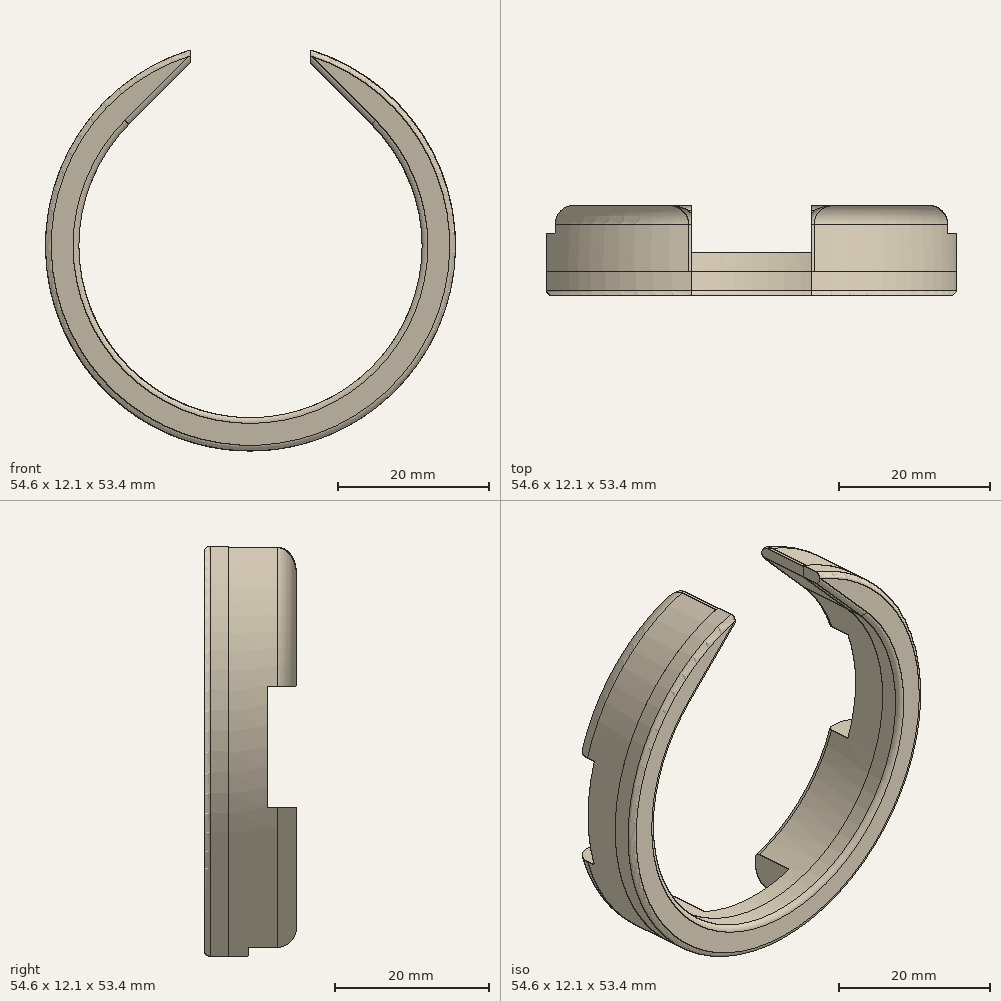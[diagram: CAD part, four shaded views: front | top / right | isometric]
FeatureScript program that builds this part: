
annotation { "Feature Type Name" : "Feature", "Feature Type Description" : "" }
export const myFeature = defineFeature(function(context is Context, id is Id, definition is map)
    precondition{}
    {
        {
            var Q0;
            Q0=qCreatedBy(makeId("Front.planeOp"),FACE);
            var sketch = newSketch(context, id + "F0", { "sketchPlane" : qUnion([Q0])});
            skArc(sketch, "E0", {"start": v(-16.16, 16.16) * mm, "mid": v(0, -22.86) * mm, "end": v(16.16, 16.16) * mm});
            skArc(sketch, "E1", {"start": v(-7.94, 26.13) * mm, "mid": v(0, -27.3) * mm, "end": v(7.94, 26.13) * mm});
            skLineSegment(sketch, "E2", {"start": v(7.94, 24.4) * mm, "end": v(7.94, 26.13) * mm});
            skLineSegment(sketch, "E3", {"start": v(0, 0) * mm, "end": v(0, 106.1) * mm, "construction": true});
            skLineSegment(sketch, "E4.MirrorCS", {"start": v(-7.94, 24.4) * mm, "end": v(-7.94, 26.13) * mm});
            skPoint(sketch, "E5.orphan", {"position": v(-7.94, 49.98) * mm});
            skPoint(sketch, "E6.orphan", {"position": v(7.94, 49.98) * mm});
            skPoint(sketch, "E7.orphan", {"position": v(7.94, 14.4) * mm});
            skPoint(sketch, "E8.orphan", {"position": v(-7.94, 14.4) * mm});
            skLineSegment(sketch, "E9", {"start": v(7.94, 24.4) * mm, "end": v(16.16, 16.16) * mm});
            skLineSegment(sketch, "E10.MirrorCS", {"start": v(-7.94, 24.4) * mm, "end": v(-16.16, 16.16) * mm});
            skPoint(sketch, "E11.orphan", {"position": v(17.29, 49.62) * mm});
            skPoint(sketch, "E12.orphan", {"position": v(-17.29, 49.62) * mm});
            skSolve(sketch);
        }
        {
            var Q0;
            Q0=makeQuery(id+"F0.imprint","IMPRINT",FACE,{"disambiguationData":[TD([[makeQuery(id+"F0.imprint","IMPRINT",EDGE,{"derivedFrom":sQuery(id+"F0.wireOp",EDGE,"E0")}),-1.0]])]});
            extrude(context, id + "F1", {"entities" : qUnion([Q0]), "depth" : 3.17 * mm});
        }
        {
            var Q0;
            Q0=makeQuery(id+"F1.opExtrude","CAP_FACE",FACE,{"disambiguationData":[OSD([sQuery(id+"F0.wireOp",EDGE,"E0"),sQuery(id+"F0.wireOp",EDGE,"E1"),sQuery(id+"F0.wireOp",EDGE,"E2"),sQuery(id+"F0.wireOp",EDGE,"E4.MirrorCS"),sQuery(id+"F0.wireOp",EDGE,"E9"),sQuery(id+"F0.wireOp",EDGE,"E10.MirrorCS")])],"isStart":true});
            extrude(context, id + "F2", {"entities" : qUnion([Q0]), "depth" : 8.9 * mm});
        }
        {
            var Q0;
            Q0=makeQuery(id+"F2.opExtrude","CAP_FACE",FACE,{"disambiguationData":[OSD([sQuery(id+"F0.wireOp",EDGE,"E0"),sQuery(id+"F0.wireOp",EDGE,"E1"),sQuery(id+"F0.wireOp",EDGE,"E2"),sQuery(id+"F0.wireOp",EDGE,"E4.MirrorCS"),sQuery(id+"F0.wireOp",EDGE,"E9"),sQuery(id+"F0.wireOp",EDGE,"E10.MirrorCS")])],"isStart":false});
            var sketch = newSketch(context, id + "F3", { "sketchPlane" : qUnion([Q0])});
            skLineSegment(sketch, "E13", {"start": v(0, 0) * mm, "end": v(0, -47.18) * mm, "construction": true});
            skLineSegment(sketch, "E14", {"start": v(-7.94, -17.24) * mm, "end": v(-7.94, -39.33) * mm});
            skLineSegment(sketch, "E15", {"start": v(-7.94, -39.33) * mm, "end": v(7.94, -39.33) * mm});
            skLineSegment(sketch, "E16", {"start": v(7.94, -39.33) * mm, "end": v(7.94, -17.24) * mm});
            skLineSegment(sketch, "E17", {"start": v(7.94, -17.24) * mm, "end": v(-7.94, -17.24) * mm});
            skLineSegment(sketch, "E18", {"start": v(0, 0) * mm, "end": v(-36.25, 0) * mm});
            skLineSegment(sketch, "E19", {"start": v(-37.48, 7.94) * mm, "end": v(-5.06, 7.94) * mm});
            skLineSegment(sketch, "E20.MirrorCS", {"start": v(-37.48, -7.94) * mm, "end": v(-5.06, -7.94) * mm});
            skLineSegment(sketch, "E21.MirrorCS", {"start": v(37.48, -7.94) * mm, "end": v(5.06, -7.94) * mm});
            skLineSegment(sketch, "E22.MirrorCS", {"start": v(37.48, 7.94) * mm, "end": v(5.06, 7.94) * mm});
            skLineSegment(sketch, "E23", {"start": v(-37.48, 7.94) * mm, "end": v(-37.48, -7.94) * mm});
            skLineSegment(sketch, "E24", {"start": v(-5.06, 7.94) * mm, "end": v(-5.06, -7.94) * mm});
            skLineSegment(sketch, "E25", {"start": v(5.06, 7.94) * mm, "end": v(5.06, -7.94) * mm});
            skLineSegment(sketch, "E26", {"start": v(37.48, 7.94) * mm, "end": v(37.48, -7.94) * mm});
            skSolve(sketch);
        }
        {
            var Q0;
            {var subQ0=sQuery(id+"F3.wireOp",EDGE,"E14");var subQ1=makeQuery(id+"F2.opExtrude","CAP_EDGE",EDGE,{"disambiguationData":[OSD([sQuery(id+"F0.wireOp",EDGE,"E0")])],"isStart":false});var subQ2=makeQuery(id+"F3.imprint","INTERSECT",VERTEX,{"derivedFrom":[subQ1,subQ0]});Q0=makeQuery(id+"F3.imprint","IMPRINT",FACE,{"disambiguationData":[TD([[makeQuery(id+"F3.imprint","IMPRINT",EDGE,{"disambiguationData":[TD([[subQ2,-1.0]])],"derivedFrom":subQ0}),1.0]])]});}
            extrude(context, id + "F4", {"entities" : qUnion([Q0]), "operationType" : NewBodyOperationType.REMOVE, "oppositeDirection" : true, "depth" : 6.35 * mm});
        }
        {
            var Q0;
            {var subQ0=sQuery(id+"F0.wireOp",EDGE,"E4.MirrorCS");var subQ1=sQuery(id+"F0.wireOp",EDGE,"E1");var subQ2=sQuery(id+"F0.wireOp",EDGE,"E10.MirrorCS");var subQ3=sQuery(id+"F0.wireOp",EDGE,"E0");Q0=makeQuery(id+"F4.boolean.opBoolean","SPLIT",FACE,{"disambiguationData":[TD([makeQuery(id+"F2.opExtrude","SWEPT_FACE",FACE,{"disambiguationData":[OSD([subQ0])]})])],"derivedFrom":makeQuery(id+"F2.opExtrude","CAP_FACE",FACE,{"disambiguationData":[OSD([subQ3,subQ1,sQuery(id+"F0.wireOp",EDGE,"E2"),subQ0,sQuery(id+"F0.wireOp",EDGE,"E9"),subQ2])],"isStart":false})});}
            var sketch = newSketch(context, id + "F5", { "sketchPlane" : qUnion([Q0])});
            skLineSegment(sketch, "E27", {"start": v(0, 0) * mm, "end": v(-60.95, 0) * mm, "construction": true});
            skLineSegment(sketch, "E28", {"start": v(-19.52, 7.94) * mm, "end": v(-29.4, 7.94) * mm});
            skLineSegment(sketch, "E29.MirrorCS", {"start": v(-19.52, -7.94) * mm, "end": v(-29.4, -7.94) * mm});
            skLineSegment(sketch, "E30", {"start": v(0, 0) * mm, "end": v(0, 37.06) * mm, "construction": true});
            skLineSegment(sketch, "E31.MirrorCS", {"start": v(19.52, 7.94) * mm, "end": v(29.4, 7.94) * mm});
            skLineSegment(sketch, "E32.MirrorCS", {"start": v(19.52, -7.94) * mm, "end": v(29.4, -7.94) * mm});
            skArc(sketch, "E33", {"start": v(-19.52, 7.94) * mm, "mid": v(-21.07, 0) * mm, "end": v(-19.52, -7.94) * mm});
            skArc(sketch, "E34", {"start": v(-29.4, 7.94) * mm, "mid": v(-30.46, 0) * mm, "end": v(-29.4, -7.94) * mm});
            skPoint(sketch, "E35.orphan", {"position": v(-67.54, 7.94) * mm});
            skPoint(sketch, "E36.orphan", {"position": v(-67.54, -7.94) * mm});
            skPoint(sketch, "E37.orphan", {"position": v(-13.33, 7.94) * mm});
            skPoint(sketch, "E38.orphan", {"position": v(-13.33, -7.94) * mm});
            skPoint(sketch, "E39.orphan", {"position": v(13.33, -7.94) * mm});
            skPoint(sketch, "E40.orphan", {"position": v(67.54, -7.94) * mm});
            skPoint(sketch, "E41.orphan", {"position": v(67.54, 7.94) * mm});
            skPoint(sketch, "E42.orphan", {"position": v(13.33, 7.94) * mm});
            skArc(sketch, "E43.trimOffspring", {"start": v(29.4, -7.94) * mm, "mid": v(30.46, 0) * mm, "end": v(29.4, 7.94) * mm});
            skArc(sketch, "E44.trimOffspring", {"start": v(19.52, -7.94) * mm, "mid": v(21.07, 0) * mm, "end": v(19.52, 7.94) * mm});
            skSolve(sketch);
        }
        {
            var Q0;
            Q0=makeQuery(id+"F5.imprint","IMPRINT",FACE,{"disambiguationData":[TD([[makeQuery(id+"F5.imprint","IMPRINT",EDGE,{"derivedFrom":sQuery(id+"F5.wireOp",EDGE,"E28")}),1.0]])]});
            var Q1;
            {var subQ0=sQuery(id+"F5.wireOp",EDGE,"E43.trimOffspring");Q1=makeQuery(id+"F5.imprint","IMPRINT",FACE,{"disambiguationData":[TD([[makeQuery(id+"F5.imprint","IMPRINT",EDGE,{"derivedFrom":subQ0}),1.0]])]});}
            var Q2;
            {var subQ0=sQuery(id+"F5.wireOp",EDGE,"E31.MirrorCS");var subQ1=sQuery(id+"F0.wireOp",EDGE,"E0");var subQ2=sQuery(id+"F0.wireOp",EDGE,"E10.MirrorCS");var subQ7=makeQuery(id+"F4.boolean.opBoolean","SPLIT",EDGE,{"disambiguationData":[TD([makeQuery(id+"F2.opExtrude","SWEPT_FACE",FACE,{"disambiguationData":[OSD([subQ2])]})])],"derivedFrom":makeQuery(id+"F2.opExtrude","CAP_EDGE",EDGE,{"disambiguationData":[OSD([subQ1])],"isStart":false})});var subQ8=makeQuery(id+"F5.imprint","INTERSECT",VERTEX,{"derivedFrom":[subQ7,subQ0]});Q2=makeQuery(id+"F5.imprint","IMPRINT",FACE,{"disambiguationData":[TD([[makeQuery(id+"F5.imprint","IMPRINT",EDGE,{"disambiguationData":[TD([[subQ8,-1.0]])],"derivedFrom":subQ0}),-1.0]])]});}
            var Q3;
            {var subQ0=sQuery(id+"F5.wireOp",EDGE,"E44.trimOffspring");Q3=makeQuery(id+"F5.imprint","IMPRINT",FACE,{"disambiguationData":[TD([[makeQuery(id+"F5.imprint","IMPRINT",EDGE,{"derivedFrom":subQ0}),-1.0]])]});}
            extrude(context, id + "F6", {"entities" : qUnion([Q0, Q1, Q2, Q3]), "operationType" : NewBodyOperationType.REMOVE, "oppositeDirection" : true, "depth" : 3.8 * mm});
        }
        {
            var Q0;
            {var subQ0=sQuery(id+"F0.wireOp",EDGE,"E1");var subQ2=sQuery(id+"F0.wireOp",EDGE,"E2");var subQ3=makeQuery(id+"F2.opExtrude","SWEPT_FACE",FACE,{"disambiguationData":[OSD([subQ2])]});Q0=makeQuery(id+"F6.boolean.opBoolean","SPLIT",EDGE,{"disambiguationData":[TD([subQ3])],"derivedFrom":makeQuery(id+"F4.boolean.opBoolean","SPLIT",EDGE,{"disambiguationData":[TD([subQ3])],"derivedFrom":makeQuery(id+"F2.opExtrude","CAP_EDGE",EDGE,{"disambiguationData":[OSD([subQ0])],"isStart":false})})});}
            var Q1;
            {var subQ0=sQuery(id+"F0.wireOp",EDGE,"E1");var subQ2=makeQuery(id+"F4.opExtrude","SWEPT_FACE",FACE,{"disambiguationData":[OSD([sQuery(id+"F3.wireOp",EDGE,"E16")])]});var subQ3=sQuery(id+"F0.wireOp",EDGE,"E4.MirrorCS");Q1=makeQuery(id+"F6.boolean.opBoolean","SPLIT",EDGE,{"disambiguationData":[TD([makeQuery(id+"F4.boolean.opBoolean","COPY",FACE,{"derivedFrom":subQ2})])],"derivedFrom":makeQuery(id+"F4.boolean.opBoolean","SPLIT",EDGE,{"disambiguationData":[TD([makeQuery(id+"F2.opExtrude","SWEPT_FACE",FACE,{"disambiguationData":[OSD([subQ3])]})])],"derivedFrom":makeQuery(id+"F2.opExtrude","CAP_EDGE",EDGE,{"disambiguationData":[OSD([subQ0])],"isStart":false})})});}
            var Q2;
            {var subQ0=sQuery(id+"F0.wireOp",EDGE,"E1");var subQ2=sQuery(id+"F0.wireOp",EDGE,"E2");var subQ4=makeQuery(id+"F4.opExtrude","SWEPT_FACE",FACE,{"disambiguationData":[OSD([sQuery(id+"F3.wireOp",EDGE,"E14")])]});Q2=makeQuery(id+"F6.boolean.opBoolean","SPLIT",EDGE,{"disambiguationData":[TD([makeQuery(id+"F4.boolean.opBoolean","COPY",FACE,{"derivedFrom":subQ4})])],"derivedFrom":makeQuery(id+"F4.boolean.opBoolean","SPLIT",EDGE,{"disambiguationData":[TD([makeQuery(id+"F2.opExtrude","SWEPT_FACE",FACE,{"disambiguationData":[OSD([subQ2])]})])],"derivedFrom":makeQuery(id+"F2.opExtrude","CAP_EDGE",EDGE,{"disambiguationData":[OSD([subQ0])],"isStart":false})})});}
            var Q3;
            {var subQ0=sQuery(id+"F0.wireOp",EDGE,"E1");var subQ2=sQuery(id+"F0.wireOp",EDGE,"E4.MirrorCS");var subQ3=makeQuery(id+"F2.opExtrude","SWEPT_FACE",FACE,{"disambiguationData":[OSD([subQ2])]});Q3=makeQuery(id+"F6.boolean.opBoolean","SPLIT",EDGE,{"disambiguationData":[TD([subQ3])],"derivedFrom":makeQuery(id+"F4.boolean.opBoolean","SPLIT",EDGE,{"disambiguationData":[TD([subQ3])],"derivedFrom":makeQuery(id+"F2.opExtrude","CAP_EDGE",EDGE,{"disambiguationData":[OSD([subQ0])],"isStart":false})})});}
            fillet(context, id + "F7", {"entities" : qUnion([Q0, Q1, Q2, Q3]), "radius" : 2.54 * mm, "tangentPropagation" : true, "allowEdgeOverflow" : false});
        }
        {
            var Q0;
            Q0=makeQuery(id+"F1.opExtrude","CAP_EDGE",EDGE,{"disambiguationData":[OSD([sQuery(id+"F0.wireOp",EDGE,"E1")])],"isStart":false});
            fillet(context, id + "F8", {"entities" : qUnion([Q0]), "radius" : 0.76 * mm, "tangentPropagation" : true, "allowEdgeOverflow" : false});
        }
        {
            var Q0;
            Q0=makeQuery(id+"F1.opExtrude","CAP_EDGE",EDGE,{"disambiguationData":[OSD([sQuery(id+"F0.wireOp",EDGE,"E0")])],"isStart":false});
            var Q1;
            Q1=makeQuery(id+"F1.opExtrude","CAP_EDGE",EDGE,{"disambiguationData":[OSD([sQuery(id+"F0.wireOp",EDGE,"E10.MirrorCS")])],"isStart":false});
            var Q2;
            Q2=makeQuery(id+"F1.opExtrude","CAP_EDGE",EDGE,{"disambiguationData":[OSD([sQuery(id+"F0.wireOp",EDGE,"E9")])],"isStart":false});
            fillet(context, id + "F9", {"entities" : qUnion([Q0, Q1, Q2]), "radius" : 0.76 * mm, "tangentPropagation" : true, "allowEdgeOverflow" : false});
        }
        {
            var Q0;
            {var subQ0=sQuery(id+"F0.wireOp",EDGE,"E0");var subQ2=sQuery(id+"F0.wireOp",EDGE,"E10.MirrorCS");var subQ3=makeQuery(id+"F2.opExtrude","SWEPT_FACE",FACE,{"disambiguationData":[OSD([subQ2])]});Q0=makeQuery(id+"F6.boolean.opBoolean","SPLIT",EDGE,{"disambiguationData":[TD([subQ3])],"derivedFrom":makeQuery(id+"F4.boolean.opBoolean","SPLIT",EDGE,{"disambiguationData":[TD([subQ3])],"derivedFrom":makeQuery(id+"F2.opExtrude","CAP_EDGE",EDGE,{"disambiguationData":[OSD([subQ0])],"isStart":false})})});}
            var Q1;
            {var subQ0=sQuery(id+"F0.wireOp",EDGE,"E0");var subQ2=sQuery(id+"F0.wireOp",EDGE,"E10.MirrorCS");var subQ4=makeQuery(id+"F4.opExtrude","SWEPT_FACE",FACE,{"disambiguationData":[OSD([sQuery(id+"F3.wireOp",EDGE,"E16")])]});Q1=makeQuery(id+"F6.boolean.opBoolean","SPLIT",EDGE,{"disambiguationData":[TD([makeQuery(id+"F4.boolean.opBoolean","COPY",FACE,{"derivedFrom":subQ4})])],"derivedFrom":makeQuery(id+"F4.boolean.opBoolean","SPLIT",EDGE,{"disambiguationData":[TD([makeQuery(id+"F2.opExtrude","SWEPT_FACE",FACE,{"disambiguationData":[OSD([subQ2])]})])],"derivedFrom":makeQuery(id+"F2.opExtrude","CAP_EDGE",EDGE,{"disambiguationData":[OSD([subQ0])],"isStart":false})})});}
            var Q2;
            {var subQ0=sQuery(id+"F0.wireOp",EDGE,"E0");var subQ2=sQuery(id+"F0.wireOp",EDGE,"E9");var subQ4=makeQuery(id+"F4.opExtrude","SWEPT_FACE",FACE,{"disambiguationData":[OSD([sQuery(id+"F3.wireOp",EDGE,"E14")])]});Q2=makeQuery(id+"F6.boolean.opBoolean","SPLIT",EDGE,{"disambiguationData":[TD([makeQuery(id+"F4.boolean.opBoolean","COPY",FACE,{"derivedFrom":subQ4})])],"derivedFrom":makeQuery(id+"F4.boolean.opBoolean","SPLIT",EDGE,{"disambiguationData":[TD([makeQuery(id+"F2.opExtrude","SWEPT_FACE",FACE,{"disambiguationData":[OSD([subQ2])]})])],"derivedFrom":makeQuery(id+"F2.opExtrude","CAP_EDGE",EDGE,{"disambiguationData":[OSD([subQ0])],"isStart":false})})});}
            var Q3;
            {var subQ0=sQuery(id+"F0.wireOp",EDGE,"E0");var subQ2=sQuery(id+"F0.wireOp",EDGE,"E9");var subQ3=makeQuery(id+"F2.opExtrude","SWEPT_FACE",FACE,{"disambiguationData":[OSD([subQ2])]});Q3=makeQuery(id+"F6.boolean.opBoolean","SPLIT",EDGE,{"disambiguationData":[TD([subQ3])],"derivedFrom":makeQuery(id+"F4.boolean.opBoolean","SPLIT",EDGE,{"disambiguationData":[TD([subQ3])],"derivedFrom":makeQuery(id+"F2.opExtrude","CAP_EDGE",EDGE,{"disambiguationData":[OSD([subQ0])],"isStart":false})})});}
            var Q4;
            Q4=makeQuery(id+"F2.opExtrude","CAP_EDGE",EDGE,{"disambiguationData":[OSD([sQuery(id+"F0.wireOp",EDGE,"E10.MirrorCS")])],"isStart":false});
            var Q5;
            Q5=makeQuery(id+"F2.opExtrude","CAP_EDGE",EDGE,{"disambiguationData":[OSD([sQuery(id+"F0.wireOp",EDGE,"E9")])],"isStart":false});
            var Q6;
            {var subQ0=sQuery(id+"F0.wireOp",EDGE,"E10.MirrorCS");var subQ1=sQuery(id+"F0.wireOp",EDGE,"E1");var subQ3=sQuery(id+"F0.wireOp",EDGE,"E4.MirrorCS");var subQ4=makeQuery(id+"F2.opExtrude","SWEPT_FACE",FACE,{"disambiguationData":[OSD([subQ3])]});Q6=makeQuery(id+"F7.opFillet","BLEND_EDGE",EDGE,{"blendedFrom":[makeQuery(id+"F6.boolean.opBoolean","SPLIT",EDGE,{"disambiguationData":[TD([subQ4])],"derivedFrom":makeQuery(id+"F4.boolean.opBoolean","SPLIT",EDGE,{"disambiguationData":[TD([subQ4])],"derivedFrom":makeQuery(id+"F2.opExtrude","CAP_EDGE",EDGE,{"disambiguationData":[OSD([subQ1])],"isStart":false})})}),makeQuery(id+"F2.opExtrude","SWEPT_FACE",FACE,{"disambiguationData":[OSD([subQ0])]})],"blendedInto":[makeQuery(id+"F2.opExtrude","SWEPT_FACE",FACE,{"disambiguationData":[OSD([subQ0])]})]});}
            var Q7;
            {var subQ0=sQuery(id+"F0.wireOp",EDGE,"E9");var subQ1=sQuery(id+"F0.wireOp",EDGE,"E1");var subQ3=sQuery(id+"F0.wireOp",EDGE,"E2");var subQ4=makeQuery(id+"F2.opExtrude","SWEPT_FACE",FACE,{"disambiguationData":[OSD([subQ3])]});Q7=makeQuery(id+"F7.opFillet","BLEND_EDGE",EDGE,{"blendedFrom":[makeQuery(id+"F6.boolean.opBoolean","SPLIT",EDGE,{"disambiguationData":[TD([subQ4])],"derivedFrom":makeQuery(id+"F4.boolean.opBoolean","SPLIT",EDGE,{"disambiguationData":[TD([subQ4])],"derivedFrom":makeQuery(id+"F2.opExtrude","CAP_EDGE",EDGE,{"disambiguationData":[OSD([subQ1])],"isStart":false})})}),makeQuery(id+"F2.opExtrude","SWEPT_FACE",FACE,{"disambiguationData":[OSD([subQ0])]})],"blendedInto":[makeQuery(id+"F2.opExtrude","SWEPT_FACE",FACE,{"disambiguationData":[OSD([subQ0])]})]});}
            fillet(context, id + "F10", {"entities" : qUnion([Q0, Q1, Q2, Q3, Q4, Q5, Q6, Q7]), "radius" : 0.76 * mm, "tangentPropagation" : true, "allowEdgeOverflow" : false});
        }
    });
